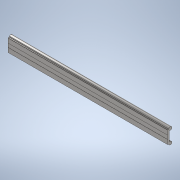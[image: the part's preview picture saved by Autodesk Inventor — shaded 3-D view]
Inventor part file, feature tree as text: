
AUTODESK INVENTOR PART (.ipt)
format: ipt  version: 2020 (Build 240168000, 168)  size: 121,856 bytes
history: native  units: mm
features: other x1, extrude x1, sketch x1
ambient origin geometry x8: Origin, YZ Plane, XZ Plane, XY Plane, X Axis, Y Axis, Z Axis, Center Point
bodies: Body1 (feature_tree)
feature tree (3):
  other  "Bryła1"
  extrude  "Wyciągnięcie proste1"  Depth=500.0mm TaperAngle=0.0deg
  sketch  "Szkic1"
